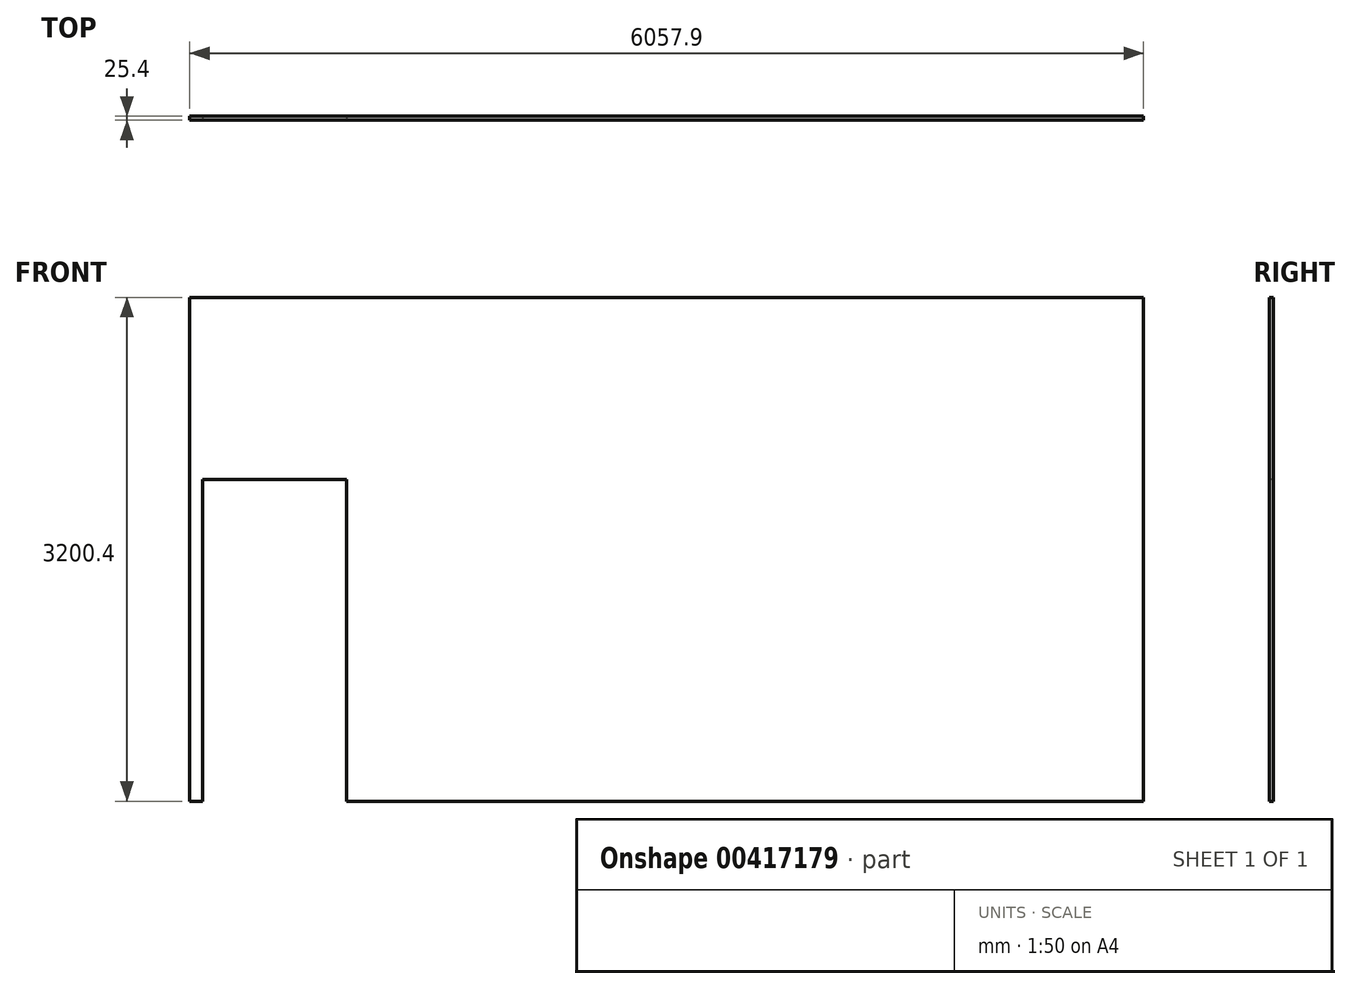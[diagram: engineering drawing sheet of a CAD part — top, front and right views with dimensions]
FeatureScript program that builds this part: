
annotation { "Feature Type Name" : "Feature", "Feature Type Description" : "" }
export const myFeature = defineFeature(function(context is Context, id is Id, definition is map)
    precondition{}
    {
        {
            var Q0;
            Q0=qCreatedBy(makeId("Front.planeOp"),FACE);
            var sketch = newSketch(context, id + "F0", { "sketchPlane" : qUnion([Q0])});
            skLineSegment(sketch, "E0.bottom", {"start": v(0, 0) * mm, "end": v(82.55, 0) * mm});
            skLineSegment(sketch, "E0.top", {"start": v(0, 3200.4) * mm, "end": v(6057.9, 3200.4) * mm});
            skLineSegment(sketch, "E0.left", {"start": v(0, 0) * mm, "end": v(0, 3200.4) * mm});
            skLineSegment(sketch, "E0.right", {"start": v(6057.9, 0) * mm, "end": v(6057.9, 3200.4) * mm});
            skLineSegment(sketch, "E1.top", {"start": v(82.55, 2044.7) * mm, "end": v(996.95, 2044.7) * mm});
            skLineSegment(sketch, "E1.left", {"start": v(82.55, 0) * mm, "end": v(82.55, 2044.7) * mm});
            skLineSegment(sketch, "E1.right", {"start": v(996.95, 0) * mm, "end": v(996.95, 2044.7) * mm});
            skLineSegment(sketch, "E2.trimOffspring", {"start": v(996.95, 0) * mm, "end": v(6057.9, 0) * mm});
            skSolve(sketch);
        }
        {
            var Q0;
            Q0=makeQuery(id+"F0.imprint","IMPRINT",FACE,{"disambiguationData":[TD([[makeQuery(id+"F0.imprint","IMPRINT",EDGE,{"derivedFrom":sQuery(id+"F0.wireOp",EDGE,"E0.bottom")}),1.0]])]});
            extrude(context, id + "F1", {"entities" : qUnion([Q0]), "oppositeDirection" : true, "depth" : 25.4 * mm});
        }
    });
